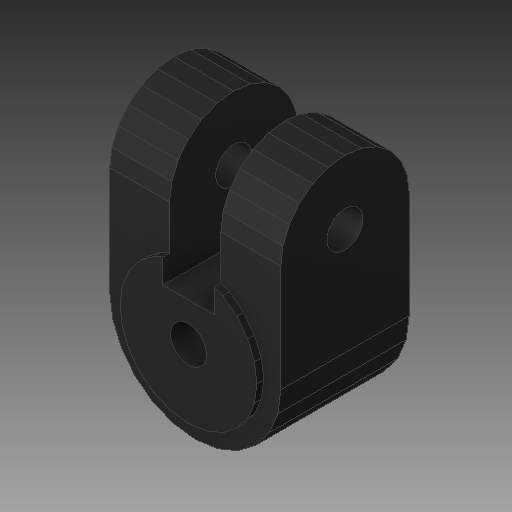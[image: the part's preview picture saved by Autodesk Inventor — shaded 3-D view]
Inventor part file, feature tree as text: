
AUTODESK INVENTOR PART (.ipt)
format: ipt  version: 2018 (Build 220112000, 112)  size: 247,296 bytes
history: native  units: mm
features: other x2, extrude x2, sketch x2
ambient origin geometry x8: Origin, YZ Plane, XZ Plane, XY Plane, X Axis, Y Axis, Z Axis, Center Point
bodies: Solid1 (feature_tree)
feature tree (6):
  other  "LCD Mount Part 2"
  other  "MeshFeature1"
  extrude  "Extrusion1"  Depth=10.0mm TaperAngle=0.0deg
  extrude  "Extrusion2"  Depth=10.0mm TaperAngle=0.0deg
  sketch  "Sketch1"  dims[d0=4.2mm d1=10.0mm d2=0.0mm]
  sketch  "Sketch2"  dims[d3=4.2mm d4=10.0mm d5=0.0mm]
